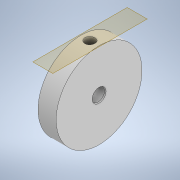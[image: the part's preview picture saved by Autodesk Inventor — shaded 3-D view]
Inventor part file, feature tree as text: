
AUTODESK INVENTOR PART (.ipt)
format: ipt  version: 2020 (Build 240168000, 168)  size: 126,976 bytes
history: native  units: mm
features: extrude x3, sketch x3, plane x1, chamfer x1
ambient origin geometry x8: Origin, YZ Plane, XZ Plane, XY Plane, X Axis, Y Axis, Z Axis, Center Point
bodies: Solid1 (feature_tree)
feature tree (8):
  extrude  "Extrusion1"  Depth=85.0mm
  plane  "Work Plane1"
  extrude  "Extrusion2"  Depth=18.0mm
  extrude  "Extrusion3"  Depth=10.0mm TaperAngle=0.0deg
  chamfer  "Chamfer1"  Distance=5.2mm
  sketch  "Sketch2"  dims[d0=12.8mm d1=85.0mm]
  sketch  "Sketch4"  dims[d2=18.0mm d3=0.0mm d5=9.0mm]
  sketch  "Sketch5"  dims[d6=10.0mm d7=22.0mm d8=0.0mm d9=5.2mm d10=22.0mm d11=0.0mm d12=0.5mm d13=2.0mm d14=11.34464mm]
